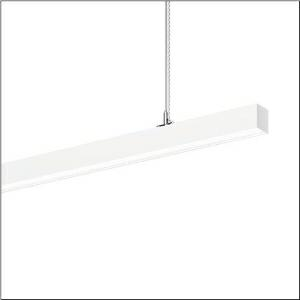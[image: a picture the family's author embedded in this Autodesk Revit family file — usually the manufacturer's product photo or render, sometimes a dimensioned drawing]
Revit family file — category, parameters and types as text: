
# Revit family: silica_r__21_51mx33tat7w_2751
name_source: partatom
category: Lighting Fixtures
units: mm (PartAtom-declared; Revit-internal decimal feet)

## family parameters
Cut with Voids When Loaded = No
Host = Face
Light Source = No
Part Type = Normal
Room Calculation Point = No
Round Connector Dimension = Use Diameter
Shared = No

## types (1)
- --- (1 x LED, 5740 lm, 53.8 W, 6500K)
    Apparent Load = 54 VA
    CIE Flux Codes = 78 96 99 56 100
    Color Rendering = 80
    Color Temperature = 6500K
    Default Elevation = 1800 mm
    Description = Silica® 21, office luminaire, primary optical cover: prismatic diffuser, of PMMA, CAT 2 (L<= 3000cd/m²), light emission: direct/indirect distribution, primary light characteristic: symmetric, installation type: suspended mounting, LED, rated luminous flux: 5.740lm, luminous efficacy: 102lm/W, light colour: 8tw, colour temperature: 2700..6500K, control gear: DALI DT8, with terminal, 3+2-pole, max. 2.5mm², mains connection: 220..240V, AC, 50/60Hz, rated input power: 56.5W, luminaire housing, of aluminium, traffic white (RAL 9016), length: 1.204mm, width: 53mm, height: 53mm, protection rating (complete): IP20, insulation class (complete): insulation class I (protective earthing), certification: CE, permissible operating ambient temperature: 0..+35°C, standard: EN 50419, packaging unit: 1 piece
    Height = 53 mm
    Lamp = 1 x LED
    Lamp Light Flux = 5740 lm
    Lamp Power = 53.8 W
    Lamp count = 1
    Length = 1204 mm
    Luminous efficacy = 107 lm/W
    Manufacturer = Siteco
    ModVariant = No
    Model = 51MX33TAT7W
    Mounting Place = Ceiling
    Mounting Type = Pendant
    Number of Poles = 1
    OnlyDefault = Yes
    Power Factor = 1
    Product Name = Silica® 21
    Product group = office luminaire | ceiling pendant
    ProductGroupID = 904
    Protection Class = Protection class I
    Protection Degree = IP 20
    RLX_Detail_Level = 1
    RLX_Emergency_Light_Flux = 0 lm
    RLX_Emergency_Type = 0
    RLX_Emergency_Type_DB = No
    RlxData = <blob elided: 18205 chars, md5=baf37ed2>
    Socket = socket
    Standby Power = 0 W
    System Light Flux = 5740 lm
    System Power = 54 W
    Type Comments = individual setting
    Type Image = l_1349007.jpg
    URL = http://relux.com
    VarID = @adj_139782
    Voltage = 0 V
    Weight = 0.00 kg
    Width = 53 mm

## geometry (parser evidence)
native form markers: Blend x4, Sweep x14
no freeform markers — native parametric forms only
